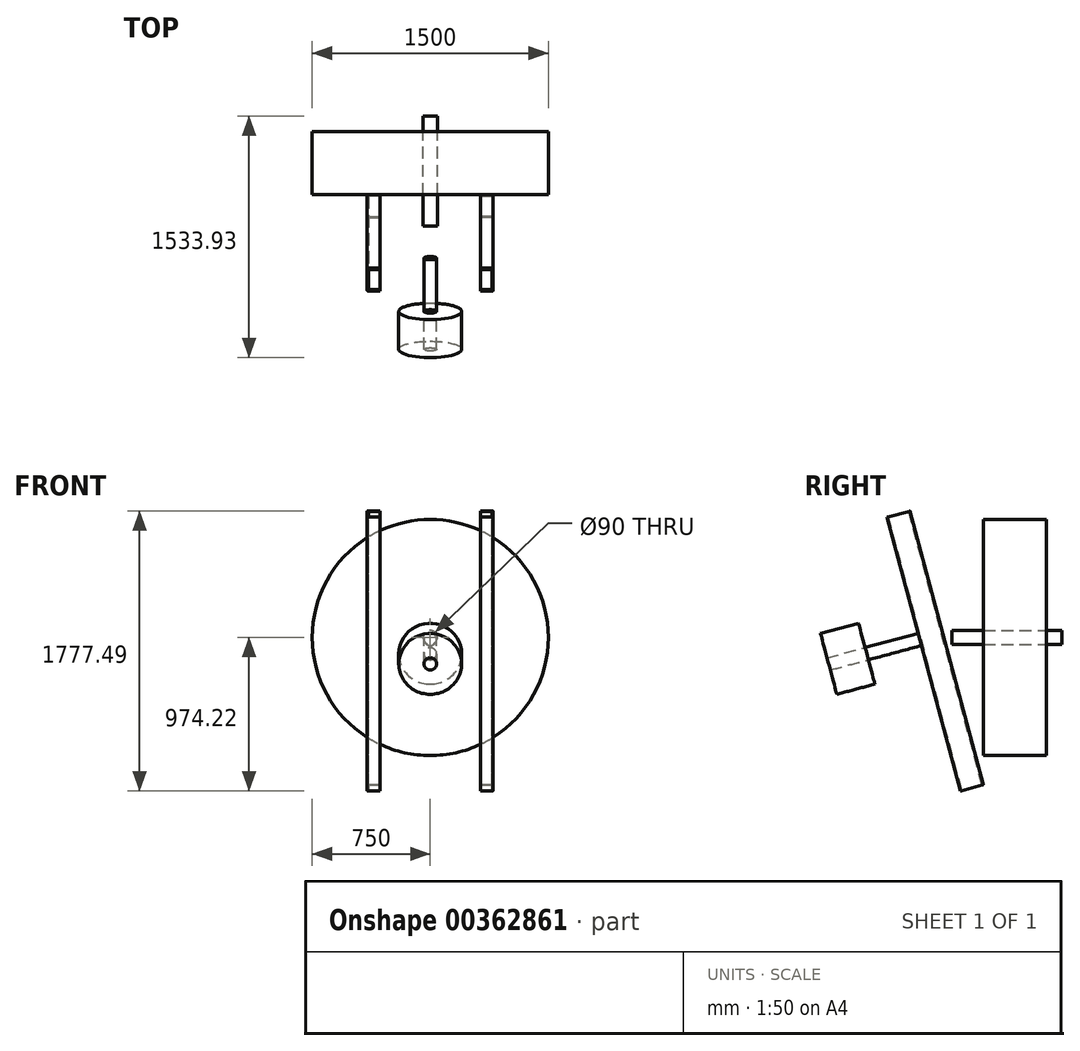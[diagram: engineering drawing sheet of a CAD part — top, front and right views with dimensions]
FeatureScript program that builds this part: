
annotation { "Feature Type Name" : "Feature", "Feature Type Description" : "" }
export const myFeature = defineFeature(function(context is Context, id is Id, definition is map)
    precondition{}
    {
        {
            var Q0;
            Q0=qCreatedBy(makeId("Front.planeOp"),FACE);
            var sketch = newSketch(context, id + "F0", { "sketchPlane" : qUnion([Q0])});
            skCircle(sketch, "E0", {"center": v(0, 0) * mm, "radius": 750 * mm});
            skCircle(sketch, "E1", {"center": v(0, 0) * mm, "radius": 45 * mm});
            skLineSegment(sketch, "E2", {"start": v(-613.55, -753.77) * mm, "end": v(721.06, -745.6) * mm, "construction": true});
            skSolve(sketch);
        }
        {
            var Q0;
            Q0 = qSketchRegion(id + "F0", true);
            extrude(context, id + "F1", {"entities" : qUnion([Q0]), "depth" : 400 * mm});
        }
        {
            var Q0;
            Q0=makeQuery(id+"F0.imprint","IMPRINT",FACE,{"disambiguationData":[TD([[makeQuery(id+"F0.imprint","IMPRINT",EDGE,{"derivedFrom":sQuery(id+"F0.wireOp",EDGE,"E1")}),1.0]])]});
            extrude(context, id + "F2", {"entities" : qUnion([Q0]), "depth" : 600 * mm, "hasSecondDirection" : true, "secondDirectionOppositeDirection" : true, "secondDirectionDepth" : 100 * mm});
        }
        {
            var Q0;
            Q0=qCreatedBy(makeId("Right.planeOp"),FACE);
            var sketch = newSketch(context, id + "F3", { "sketchPlane" : qUnion([Q0])});
            skLineSegment(sketch, "E3", {"start": v(0, 0) * mm, "end": v(0, -786.63) * mm});
            skLineSegment(sketch, "E4", {"start": v(-400, -935.4) * mm, "end": v(-400, 1064.6) * mm, "construction": true});
            skLineSegment(sketch, "E5", {"start": v(-400, -935.4) * mm, "end": v(-917.64, 996.45) * mm, "construction": true});
            skArc(sketch, "E6", {"start": v(-400, 1064.6) * mm, "mid": v(-661.05, 1047.49) * mm, "end": v(-917.64, 996.45) * mm, "construction": true});
            skLineSegment(sketch, "E7", {"start": v(-400, -935.4) * mm, "end": v(-865.87, 803.27) * mm});
            skLineSegment(sketch, "E8", {"start": v(-865.87, 803.27) * mm, "end": v(-1010.76, 764.44) * mm});
            skLineSegment(sketch, "E9", {"start": v(-1010.76, 764.44) * mm, "end": v(-544.89, -974.22) * mm});
            skLineSegment(sketch, "E10", {"start": v(-544.89, -974.22) * mm, "end": v(-400, -935.4) * mm});
            skLineSegment(sketch, "E11", {"start": v(-400, -935.4) * mm, "end": v(-400, -935.4) * mm});
            skSolve(sketch);
        }
        {
            var Q0;
            Q0=makeQuery(id+"F3.imprint","IMPRINT",FACE,{"disambiguationData":[TD([[makeQuery(id+"F3.imprint","IMPRINT",EDGE,{"derivedFrom":sQuery(id+"F3.wireOp",EDGE,"E7")}),1.0]])]});
            extrude(context, id + "F4", {"entities" : qUnion([Q0]), "depth" : 400 * mm, "hasSecondDirection" : true, "secondDirectionOppositeDirection" : true, "secondDirectionDepth" : -320 * mm});
        }
        {
            var Q0;
            Q0=makeQuery(id+"F4.opExtrude","SWEPT_FACE",FACE,{"disambiguationData":[OSD([sQuery(id+"F3.wireOp",EDGE,"E8")])]});
            var sketch = newSketch(context, id + "F5", { "sketchPlane" : qUnion([Q0])});
            skLineSegment(sketch, "E12", {"start": v(320, -636.47) * mm, "end": v(392, -636.47) * mm});
            skLineSegment(sketch, "E13", {"start": v(392, -636.47) * mm, "end": v(392, -770.47) * mm});
            skLineSegment(sketch, "E14", {"start": v(392, -770.47) * mm, "end": v(320, -770.47) * mm});
            skSolve(sketch);
        }
        {
            var Q0;
            Q0=makeQuery(id+"F5.imprint","IMPRINT",FACE,{"disambiguationData":[TD([[makeQuery(id+"F5.imprint","IMPRINT",EDGE,{"derivedFrom":sQuery(id+"F5.wireOp",EDGE,"E12")}),-1.0]])]});
            extrude(context, id + "F6", {"entities" : qUnion([Q0]), "operationType" : NewBodyOperationType.REMOVE, "endBound" : BoundingType.THROUGH_ALL, "oppositeDirection" : true, "depth" : 25 * mm});
        }
        {
            var Q0;
            Q0=makeQuery(id+"F6.boolean.opBoolean","COPY",EDGE,{"derivedFrom":makeQuery(id+"F6.opExtrude","SWEPT_EDGE",EDGE,{"disambiguationData":[OSD([sQuery(id+"F5.wireOp",EDGE,"E13"),sQuery(id+"F5.wireOp",EDGE,"E14")])]})});
            var Q1;
            Q1=makeQuery(id+"F6.boolean.opBoolean","COPY",EDGE,{"derivedFrom":makeQuery(id+"F6.opExtrude","SWEPT_EDGE",EDGE,{"disambiguationData":[OSD([sQuery(id+"F5.wireOp",EDGE,"E12"),sQuery(id+"F5.wireOp",EDGE,"E13")])]})});
            var Q2;
            Q2=makeQuery(id+"F4.opExtrude","CAP_EDGE",EDGE,{"disambiguationData":[OSD([sQuery(id+"F3.wireOp",EDGE,"E9")])],"isStart":false});
            var Q3;
            Q3=makeQuery(id+"F4.opExtrude","CAP_EDGE",EDGE,{"disambiguationData":[OSD([sQuery(id+"F3.wireOp",EDGE,"E7")])],"isStart":false});
            fillet(context, id + "F7", {"entities" : qUnion([Q0, Q1, Q2, Q3]), "radius" : 5 * mm, "tangentPropagation" : true, "allowEdgeOverflow" : false});
        }
        {
            var Q0;
            Q0=makeQuery(id+"F4.opExtrude","SWEPT_BODY",BODY,{"disambiguationData":[OSD([sQuery(id+"F3.wireOp",EDGE,"E7"),sQuery(id+"F3.wireOp",EDGE,"E8"),sQuery(id+"F3.wireOp",EDGE,"E9"),sQuery(id+"F3.wireOp",EDGE,"E10")])]});
            var Q1;
            Q1=makeQuery(id+"F3.imprint","IMPRINT",FACE,{"disambiguationData":[TD([[makeQuery(id+"F3.imprint","IMPRINT",EDGE,{"derivedFrom":sQuery(id+"F3.wireOp",EDGE,"E7")}),1.0]])]});
            mirror(context, id + "F8", {"entities" : qUnion([Q0]), "mirrorPlane" : qUnion([Q1])});
        }
        {
            var Q0;
            Q0=qCreatedBy(makeId("Right.planeOp"),FACE);
            var sketch = newSketch(context, id + "F9", { "sketchPlane" : qUnion([Q0])});
            skLineSegment(sketch, "E15", {"start": v(-1267.39, 0) * mm, "end": v(0, 0) * mm, "construction": true});
            skLineSegment(sketch, "E16.0", {"start": v(-1010.76, 764.44) * mm, "end": v(-544.89, -974.22) * mm, "construction": true});
            skLineSegment(sketch, "E17", {"start": v(-496.79, 64.6) * mm, "end": v(-2174.62, -384.97) * mm, "construction": true});
            skSolve(sketch);
        }
        {
            var Q0;
            Q0=makeQuery(id+"F8.opPattern","COPY",FACE,{"derivedFrom":makeQuery(id+"F4.opExtrude","SWEPT_FACE",FACE,{"disambiguationData":[OSD([sQuery(id+"F3.wireOp",EDGE,"E9")])]}),"instanceName":"1"});
            var sketch = newSketch(context, id + "F10", { "sketchPlane" : qUnion([Q0])});
            skLineSegment(sketch, "E18.0", {"start": v(0, 1000) * mm, "end": v(0, -800) * mm, "construction": true});
            skLineSegment(sketch, "E19", {"start": v(-1055.5, 195.77) * mm, "end": v(1077.36, 195.77) * mm, "construction": true});
            skCircle(sketch, "E20", {"center": v(0, 195.77) * mm, "radius": 40 * mm});
            skSolve(sketch);
        }
        {
            var Q0;
            Q0 = qSketchRegion(id + "F10", true);
            extrude(context, id + "F11", {"entities" : qUnion([Q0]), "depth" : 600 * mm});
        }
        {
            var Q0;
            Q0=makeQuery(id+"F11.opExtrude","CAP_FACE",FACE,{"disambiguationData":[OSD([sQuery(id+"F10.wireOp",EDGE,"E20")])],"isStart":false});
            var sketch = newSketch(context, id + "F12", { "sketchPlane" : qUnion([Q0])});
            skLineSegment(sketch, "E21.0", {"start": v(0, 1000) * mm, "end": v(0, -800) * mm, "construction": true});
            skCircle(sketch, "E22.0", {"center": v(0, 195.77) * mm, "radius": 40 * mm});
            skCircle(sketch, "E23", {"center": v(0, 195.77) * mm, "radius": 200 * mm});
            skSolve(sketch);
        }
        {
            var Q0;
            Q0=makeQuery(id+"F12.imprint","IMPRINT",FACE,{"disambiguationData":[TD([[makeQuery(id+"F12.imprint","IMPRINT",EDGE,{"derivedFrom":sQuery(id+"F12.wireOp",EDGE,"E22.0")}),-1.0]])]});
            extrude(context, id + "F13", {"entities" : qUnion([Q0]), "depth" : -250 * mm});
        }
    });
